# Revit family: highbay_42-s_51hp327a4fma
name_source: partatom
category: Lighting Fixtures
units: mm (PartAtom-declared; Revit-internal decimal feet)

## family parameters
Cut with Voids When Loaded = No
Host = Face
Light Source = No
Part Type = Normal
Room Calculation Point = No
Round Connector Dimension = Use Diameter
Shared = No

## types (1)
- Highbay 42-S (1 x LED, 12800 lm, 80 W, 4000K)
    Apparent Load = 80 VA
    CIE Flux Codes = 49 82 98 100 100
    Color Rendering = 80
    Color Temperature = 4000K
    Default Elevation = 1800 mm
    Description = Highbay 42-S, high bay luminaire, primary light control with lens, of PC, primary optical cover: cover panel, of PC, transparent, light emission: direct distribution, primary light characteristic: rotationally symmetric, installation type: suspended mounting, surface-mounted, LED, rated luminous flux: 12.800lm, luminous efficacy: 160lm/W, light colour: 840, colour temperature: 4000K, control gear: ON/OFF, with cable, 3x 1.0mm², free wire ends, mains connection: 230V, AC, 50Hz, cable length: 1,5m, rated input power: 80W, housing, rotationally symmetric, of diecast aluminium, black, with hook on luminaire side, diameter: 275mm, height: 117mm, protection rating (complete): IP65, insulation class (complete): insulation class I (protective earthing), certification: CE, UKCA, protection symbol: D, impact resistance: IK08, permissible operating ambient temperature: -20..+40°C, corresponds to IFS (International Featured Standards) requirements for safety and quality in the food industry, packaging unit: 1 piece
    Height = 117 mm
    Lamp = 1 x LED
    Lamp Light Flux = 12800 lm
    Lamp Power = 80 W
    Lamp count = 1
    Length = 295 mm
    Luminous efficacy = 160 lm/W
    Manufacturer = Siteco
    ModVariant = No
    Model = 51HP327A4FMA
    Mounting Place = Ceiling
    Mounting Type = Pendant
    Number of Poles = 1
    OnlyDefault = Yes
    Power Factor = 1
    Product Name = Highbay 42-S
    Product group = high bay luminaire
    ProductGroupID = 901
    Protection Class = Protection class I
    Protection Degree = IP 65
    RLX_Detail_Level = 1
    RLX_Emergency_Light_Flux = 0 lm
    RLX_Emergency_Type = 0
    RLX_Emergency_Type_DB = No
    RlxData = <blob elided: 278249 chars, md5=754e542e>
    Socket = socket
    Standby Power = 0 W
    System Light Flux = 12800 lm
    System Power = 80 W
    Type Comments = Product without accessories
    Type Image = l_1003925.jpg
    URL = http://relux.com
    VarID = ---
    Voltage = 0 V
    Weight = 0.00 kg
    Width = 0 mm  [stored 0 ft]

note: [stored X ft] marks values corroborated as IEEE doubles in the binary element streams (Revit-internal decimal feet)

## geometry (parser evidence)
native form markers: Sweep x10
no freeform markers — native parametric forms only
